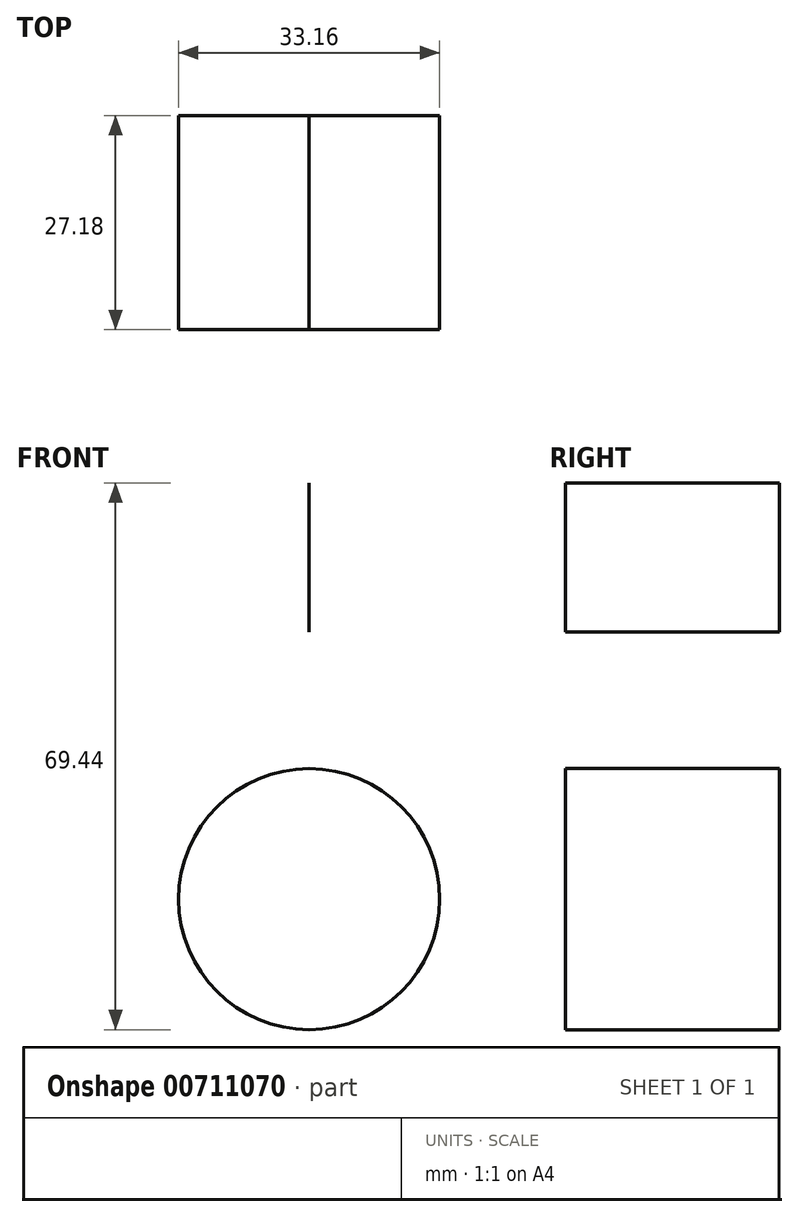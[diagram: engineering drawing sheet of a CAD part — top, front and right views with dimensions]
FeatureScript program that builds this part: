
annotation { "Feature Type Name" : "Feature", "Feature Type Description" : "" }
export const myFeature = defineFeature(function(context is Context, id is Id, definition is map)
    precondition{}
    {
        {
            var Q0;
            Q0=qCreatedBy(makeId("Front.planeOp"),FACE);
            var sketch = newSketch(context, id + "F0", { "sketchPlane" : qUnion([Q0])});
            skArc(sketch, "E0", {"start": v(0, 33.94) * mm, "mid": v(-24, -24) * mm, "end": v(33.94, 0) * mm});
            skLineSegment(sketch, "E1", {"start": v(0, 33.94) * mm, "end": v(0, 52.86) * mm});
            skLineSegment(sketch, "E2", {"start": v(0, 52.86) * mm, "end": v(66.33, 51.61) * mm});
            skLineSegment(sketch, "E3", {"start": v(66.33, 51.61) * mm, "end": v(66.33, 0) * mm});
            skLineSegment(sketch, "E4", {"start": v(66.33, 0) * mm, "end": v(33.94, 0) * mm});
            skCircle(sketch, "E5", {"center": v(0, 0) * mm, "radius": 16.58 * mm});
            skLineSegment(sketch, "E6", {"start": v(0, 33.94) * mm, "end": v(33.77, 33.94) * mm});
            skLineSegment(sketch, "E7", {"start": v(33.77, 33.94) * mm, "end": v(33.94, 0) * mm});
            skSolve(sketch);
        }
        {
            var Q0;
            Q0=sQuery(id+"F0.wireOp",EDGE,"E1");
            var Q1;
            Q1=sQuery(id+"F0.wireOp",EDGE,"E5");
            extrude(context, id + "F1", {"bodyType" : ToolBodyType.SURFACE, "surfaceEntities" : qUnion([Q0, Q1]), "depth" : 27.18 * mm, "offsetDistance" : 25.4 * mm});
        }
    });
